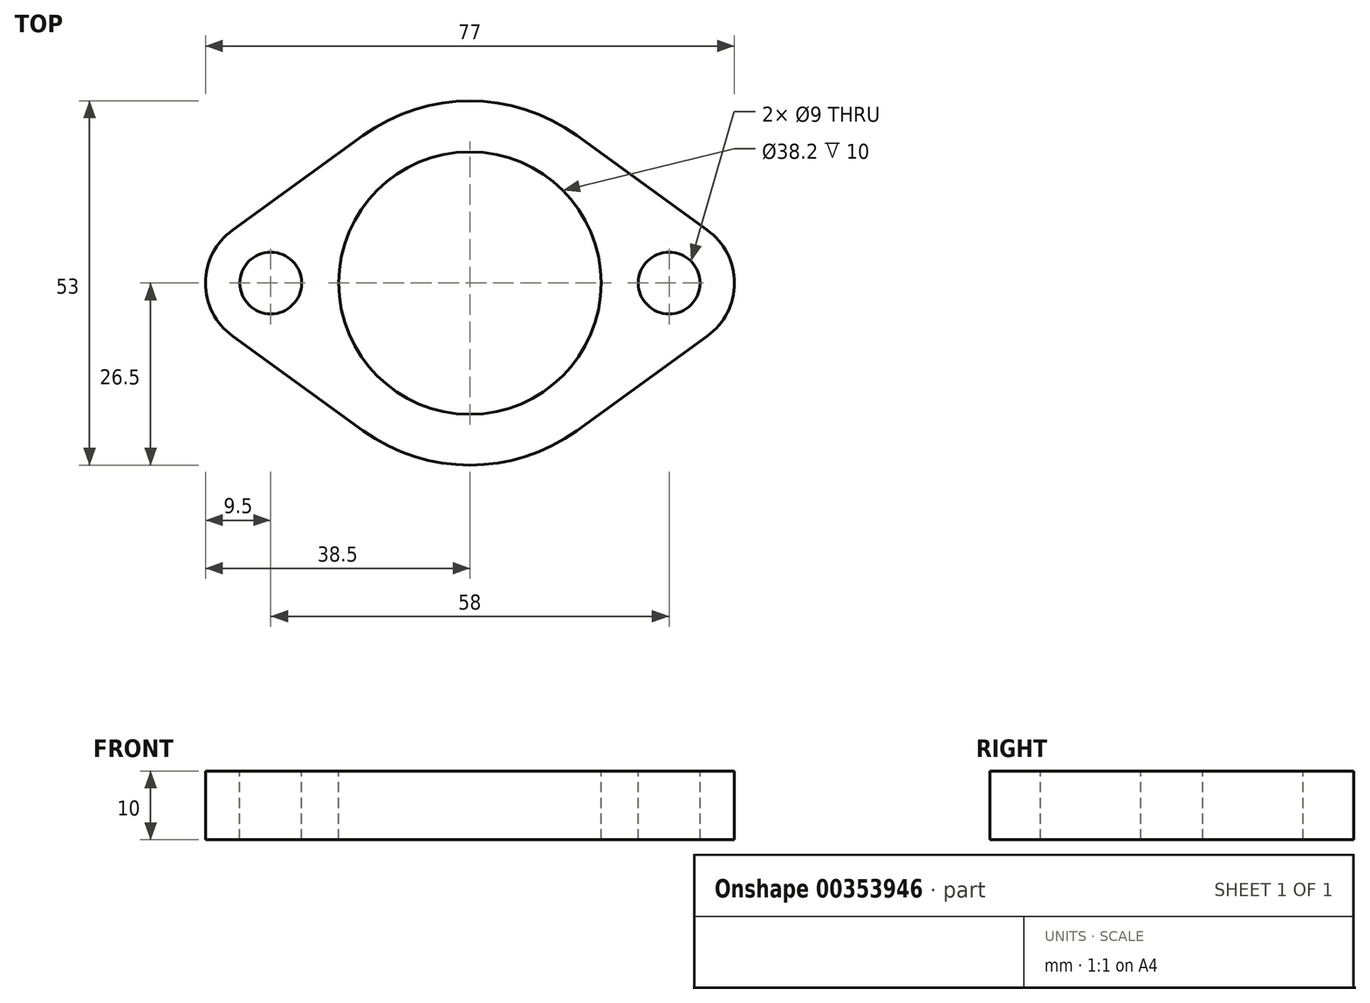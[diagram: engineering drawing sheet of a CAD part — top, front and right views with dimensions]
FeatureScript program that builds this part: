
annotation { "Feature Type Name" : "Feature", "Feature Type Description" : "" }
export const myFeature = defineFeature(function(context is Context, id is Id, definition is map)
    precondition{}
    {
        {
            var Q0;
            Q0=qCreatedBy(makeId("Top.planeOp"),FACE);
            var sketch = newSketch(context, id + "F0", { "sketchPlane" : qUnion([Q0])});
            skLineSegment(sketch, "E0", {"start": v(-29, 0) * mm, "end": v(29, 0) * mm, "construction": true});
            skArc(sketch, "E1", {"start": v(-34.57, 7.7) * mm, "mid": v(-38.5, 0) * mm, "end": v(-34.57, -7.7) * mm});
            skArc(sketch, "E2", {"start": v(34.57, -7.7) * mm, "mid": v(38.5, 0) * mm, "end": v(34.57, 7.7) * mm});
            skArc(sketch, "E3", {"start": v(-15.53, -21.47) * mm, "mid": v(0, -26.5) * mm, "end": v(15.53, -21.47) * mm});
            skLineSegment(sketch, "E4", {"start": v(15.53, 21.47) * mm, "end": v(34.57, 7.7) * mm});
            skLineSegment(sketch, "E5", {"start": v(-15.53, 21.47) * mm, "end": v(-34.57, 7.7) * mm});
            skLineSegment(sketch, "E6.MirrorCS", {"start": v(-15.53, -21.47) * mm, "end": v(-34.57, -7.7) * mm});
            skLineSegment(sketch, "E7.MirrorCS", {"start": v(15.53, -21.47) * mm, "end": v(34.57, -7.7) * mm});
            skArc(sketch, "E8.trimOffspring", {"start": v(15.53, 21.47) * mm, "mid": v(0, 26.5) * mm, "end": v(-15.53, 21.47) * mm});
            skSolve(sketch);
        }
        {
            var Q0;
            Q0 = qSketchRegion(id + "F0", true);
            extrude(context, id + "F1", {"entities" : qUnion([Q0]), "depth" : 10 * mm});
        }
        {
            var Q0;
            Q0=makeQuery(id+"F1.opExtrude","CAP_FACE",FACE,{"disambiguationData":[OSD([sQuery(id+"F0.wireOp",EDGE,"E1"),sQuery(id+"F0.wireOp",EDGE,"E2"),sQuery(id+"F0.wireOp",EDGE,"E3"),sQuery(id+"F0.wireOp",EDGE,"E4"),sQuery(id+"F0.wireOp",EDGE,"E5"),sQuery(id+"F0.wireOp",EDGE,"E6.MirrorCS"),sQuery(id+"F0.wireOp",EDGE,"E7.MirrorCS"),sQuery(id+"F0.wireOp",EDGE,"E8.trimOffspring")])],"isStart":false});
            var sketch = newSketch(context, id + "F2", { "sketchPlane" : qUnion([Q0])});
            skPoint(sketch, "E9", {"position": v(-29, 0) * mm});
            skPoint(sketch, "E10", {"position": v(29, 0) * mm});
            skSolve(sketch);
        }
        {
            var Q0;
            Q0=sQuery(id+"F2.wireOp",VERTEX,"E9");
            var Q1;
            Q1=sQuery(id+"F2.wireOp",VERTEX,"E10");
            var Q2;
            Q2=makeQuery(id+"F1.opExtrude","SWEPT_BODY",BODY,{"disambiguationData":[OSD([sQuery(id+"F0.wireOp",EDGE,"E1"),sQuery(id+"F0.wireOp",EDGE,"E2"),sQuery(id+"F0.wireOp",EDGE,"E3"),sQuery(id+"F0.wireOp",EDGE,"E4"),sQuery(id+"F0.wireOp",EDGE,"E5"),sQuery(id+"F0.wireOp",EDGE,"E6.MirrorCS"),sQuery(id+"F0.wireOp",EDGE,"E7.MirrorCS"),sQuery(id+"F0.wireOp",EDGE,"E8.trimOffspring")])]});
            hole(context, id + "F3", {"style" : HoleStyle.SIMPLE, "endStyle" : HoleEndStyle.THROUGH, "standardTappedOrClearance" : lookupTablePath({ "standard" : "ISO", "size" : "9", "type" : "Drilled" }), "standardBlindInLast" : lookupTablePath({ "standard" : "ISO", "size" : "9", "type" : "Drilled" }), "holeDiameter" : 9 * mm, "isTappedThrough" : true, "tappedDepth" : 12 * mm, "tapClearance" : 3, "locations" : qUnion([Q0, Q1]), "scope" : qUnion([Q2])});
        }
        {
            var Q0;
            Q0=makeQuery(id+"F1.opExtrude","CAP_FACE",FACE,{"disambiguationData":[OSD([sQuery(id+"F0.wireOp",EDGE,"E1"),sQuery(id+"F0.wireOp",EDGE,"E2"),sQuery(id+"F0.wireOp",EDGE,"E3"),sQuery(id+"F0.wireOp",EDGE,"E4"),sQuery(id+"F0.wireOp",EDGE,"E5"),sQuery(id+"F0.wireOp",EDGE,"E6.MirrorCS"),sQuery(id+"F0.wireOp",EDGE,"E7.MirrorCS"),sQuery(id+"F0.wireOp",EDGE,"E8.trimOffspring")])],"isStart":false});
            var sketch = newSketch(context, id + "F4", { "sketchPlane" : qUnion([Q0])});
            skCircle(sketch, "E11", {"center": v(0, 0) * mm, "radius": 19.1 * mm});
            skSolve(sketch);
        }
        {
            var Q0;
            Q0=makeQuery(id+"F4.imprint","IMPRINT",FACE,{"disambiguationData":[TD([[makeQuery(id+"F4.imprint","IMPRINT",EDGE,{"derivedFrom":sQuery(id+"F4.wireOp",EDGE,"E11")}),1.0]])]});
            extrude(context, id + "F5", {"entities" : qUnion([Q0]), "operationType" : NewBodyOperationType.REMOVE, "endBound" : BoundingType.UP_TO_NEXT, "oppositeDirection" : true, "depth" : 25 * mm});
        }
    });
